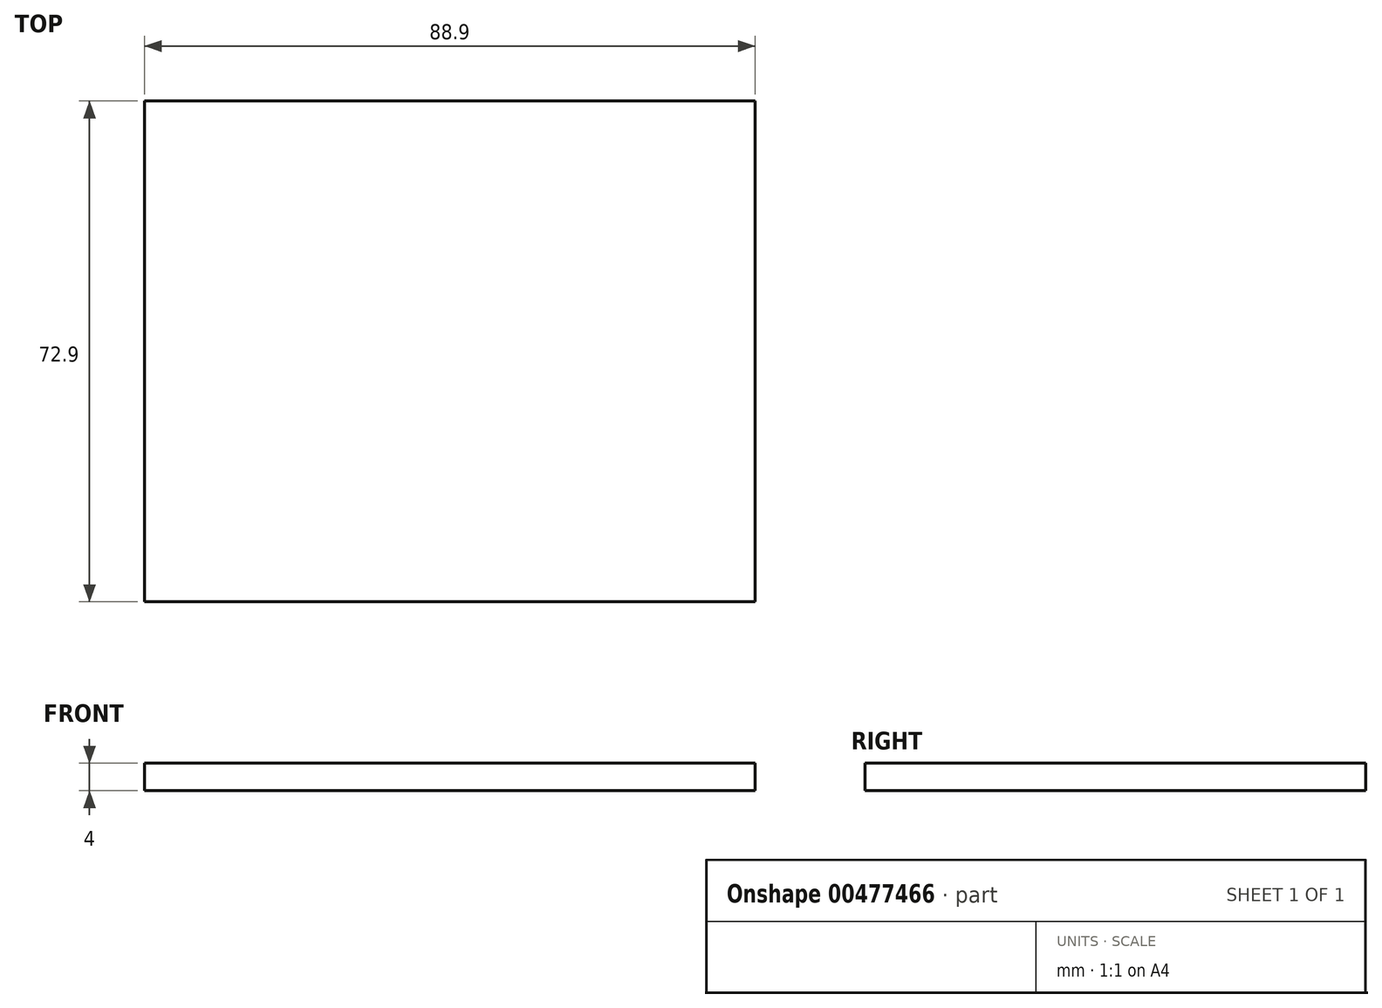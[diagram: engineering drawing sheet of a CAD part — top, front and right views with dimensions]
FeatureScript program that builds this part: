
annotation { "Feature Type Name" : "Feature", "Feature Type Description" : "" }
export const myFeature = defineFeature(function(context is Context, id is Id, definition is map)
    precondition{}
    {
        {
            var Q0;
            Q0=qCreatedBy(makeId("Top.planeOp"),FACE);
            var sketch = newSketch(context, id + "F0", { "sketchPlane" : qUnion([Q0])});
            skLineSegment(sketch, "E0.bottom", {"start": v(-49.82, 29.63) * mm, "end": v(39.08, 29.63) * mm});
            skLineSegment(sketch, "E0.top", {"start": v(-49.82, -43.27) * mm, "end": v(39.08, -43.27) * mm});
            skLineSegment(sketch, "E0.left", {"start": v(-49.82, 29.63) * mm, "end": v(-49.82, -43.27) * mm});
            skLineSegment(sketch, "E0.right", {"start": v(39.08, 29.63) * mm, "end": v(39.08, -43.27) * mm});
            skSolve(sketch);
        }
        {
            var Q0;
            Q0 = qSketchRegion(id + "F0", true);
            extrude(context, id + "F1", {"entities" : qUnion([Q0]), "depth" : 4 * mm});
        }
    });
